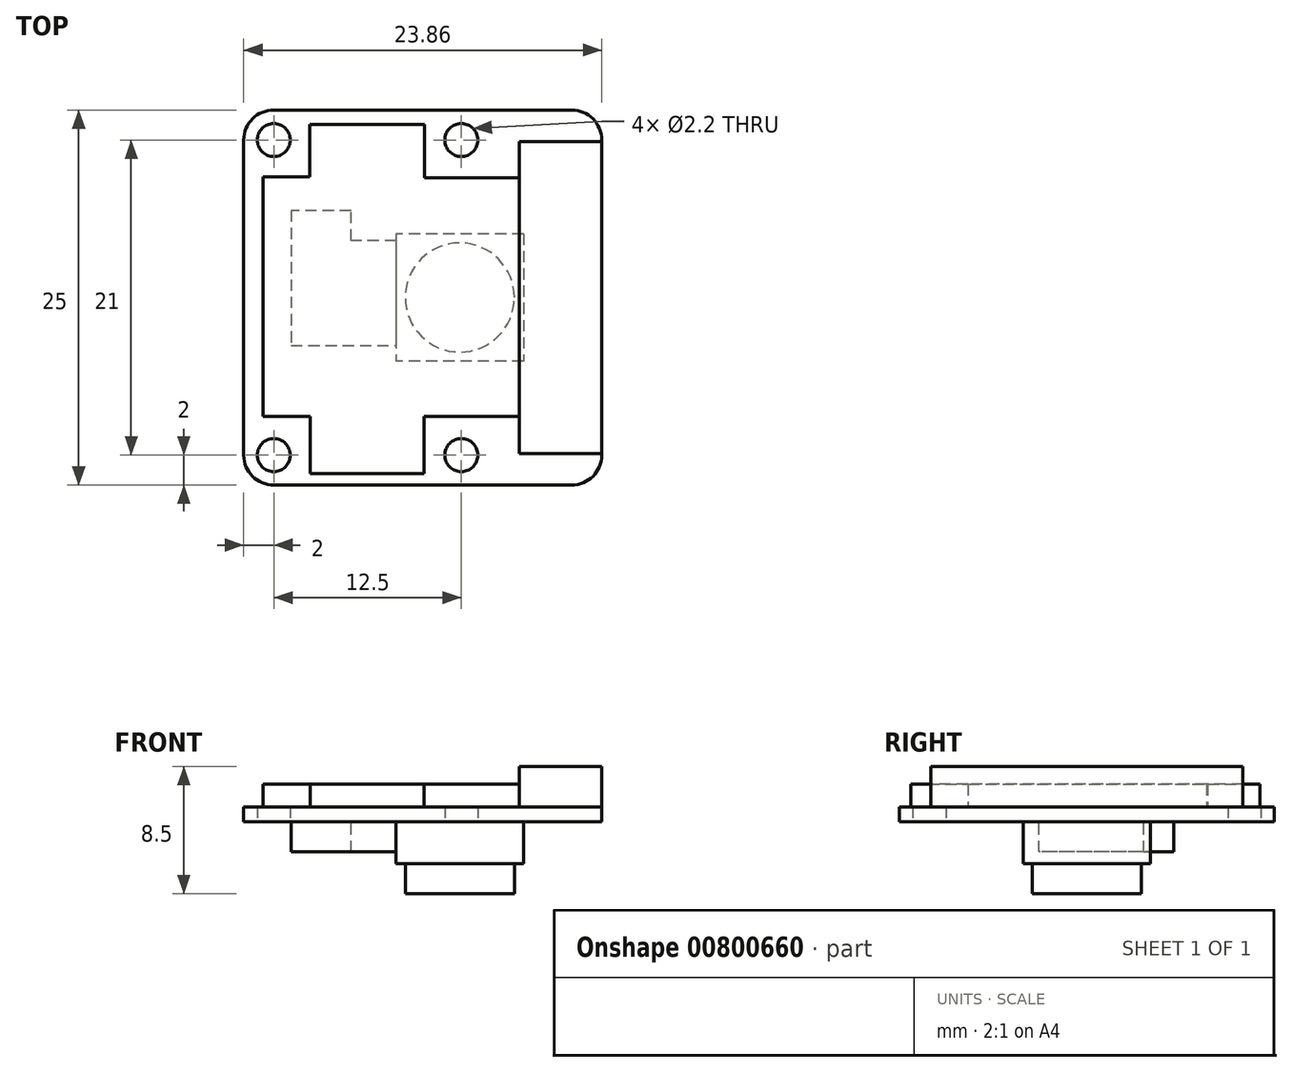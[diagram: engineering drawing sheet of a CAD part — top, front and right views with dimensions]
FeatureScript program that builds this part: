
annotation { "Feature Type Name" : "Feature", "Feature Type Description" : "" }
export const myFeature = defineFeature(function(context is Context, id is Id, definition is map)
    precondition{}
    {
        {
            var Q0;
            Q0=qCreatedBy(makeId("Top.planeOp"),FACE);
            var sketch = newSketch(context, id + "F0", { "sketchPlane" : qUnion([Q0])});
            skLineSegment(sketch, "E0.bottom", {"start": v(2, 25) * mm, "end": v(21.86, 25) * mm});
            skLineSegment(sketch, "E0.top", {"start": v(2, 0) * mm, "end": v(21.86, 0) * mm});
            skLineSegment(sketch, "E0.left", {"start": v(0, 23) * mm, "end": v(0, 2) * mm});
            skLineSegment(sketch, "E0.right", {"start": v(23.86, 23) * mm, "end": v(23.86, 2) * mm});
            skCircle(sketch, "E1", {"center": v(2, 2) * mm, "radius": 1.1 * mm});
            skCircle(sketch, "E2", {"center": v(2, 23) * mm, "radius": 1.1 * mm});
            skCircle(sketch, "E3", {"center": v(14.5, 23) * mm, "radius": 1.1 * mm});
            skCircle(sketch, "E4", {"center": v(14.5, 2) * mm, "radius": 1.1 * mm});
            skPoint(sketch, "E5.visualSharp", {"position": v(0, 0) * mm});
            skArc(sketch, "E5.filletArc", {"start": v(0, 2) * mm, "mid": v(0.59, 0.59) * mm, "end": v(2, 0) * mm});
            skPoint(sketch, "E6.visualSharp", {"position": v(0, 25) * mm});
            skArc(sketch, "E6.filletArc", {"start": v(2, 25) * mm, "mid": v(0.59, 24.41) * mm, "end": v(0, 23) * mm});
            skPoint(sketch, "E7.visualSharp", {"position": v(23.86, 25) * mm});
            skArc(sketch, "E7.filletArc", {"start": v(23.86, 23) * mm, "mid": v(23.28, 24.41) * mm, "end": v(21.86, 25) * mm});
            skPoint(sketch, "E8.visualSharp", {"position": v(23.86, 0) * mm});
            skArc(sketch, "E8.filletArc", {"start": v(21.86, 0) * mm, "mid": v(23.28, 0.59) * mm, "end": v(23.86, 2) * mm});
            skSolve(sketch);
        }
        {
            var Q0;
            Q0=makeQuery(id+"F0.imprint","IMPRINT",FACE,{"disambiguationData":[TD([[makeQuery(id+"F0.imprint","IMPRINT",EDGE,{"derivedFrom":sQuery(id+"F0.wireOp",EDGE,"E0.bottom")}),-1.0]])]});
            extrude(context, id + "F1", {"entities" : qUnion([Q0]), "depth" : 1 * mm, "offsetDistance" : 25 * mm});
        }
        {
            var Q0;
            Q0=makeQuery(id+"F1.opExtrude","CAP_FACE",FACE,{"disambiguationData":[OSD([sQuery(id+"F0.wireOp",EDGE,"E0.bottom"),sQuery(id+"F0.wireOp",EDGE,"E0.top"),sQuery(id+"F0.wireOp",EDGE,"E0.left"),sQuery(id+"F0.wireOp",EDGE,"E0.right"),sQuery(id+"F0.wireOp",EDGE,"E1"),sQuery(id+"F0.wireOp",EDGE,"E2"),sQuery(id+"F0.wireOp",EDGE,"E3"),sQuery(id+"F0.wireOp",EDGE,"E4"),sQuery(id+"F0.wireOp",EDGE,"E5.filletArc"),sQuery(id+"F0.wireOp",EDGE,"E6.filletArc"),sQuery(id+"F0.wireOp",EDGE,"E7.filletArc"),sQuery(id+"F0.wireOp",EDGE,"E8.filletArc")])],"isStart":false});
            var sketch = newSketch(context, id + "F2", { "sketchPlane" : qUnion([Q0])});
            skLineSegment(sketch, "E9.0", {"start": v(23.86, 23) * mm, "end": v(23.86, 2) * mm});
            skLineSegment(sketch, "E10.0", {"start": v(2, 0) * mm, "end": v(21.86, 0) * mm});
            skLineSegment(sketch, "E11.0", {"start": v(0, 23) * mm, "end": v(0, 2) * mm});
            skLineSegment(sketch, "E12.bottom", {"start": v(23.86, 22.9) * mm, "end": v(18.36, 22.9) * mm});
            skLineSegment(sketch, "E12.top", {"start": v(23.86, 2.1) * mm, "end": v(18.36, 2.1) * mm});
            skLineSegment(sketch, "E12.left", {"start": v(23.86, 22.9) * mm, "end": v(23.86, 2.1) * mm});
            skLineSegment(sketch, "E12.right", {"start": v(18.36, 22.9) * mm, "end": v(18.36, 2.1) * mm});
            skPoint(sketch, "E13", {"position": v(23.86, 12.5) * mm});
            skLineSegment(sketch, "E14", {"start": v(1.28, 4.59) * mm, "end": v(1.28, 20.55) * mm});
            skLineSegment(sketch, "E15", {"start": v(1.28, 20.55) * mm, "end": v(4.4, 20.55) * mm});
            skLineSegment(sketch, "E16", {"start": v(4.4, 20.55) * mm, "end": v(4.4, 24.04) * mm});
            skLineSegment(sketch, "E17", {"start": v(4.4, 24.04) * mm, "end": v(12.06, 24.04) * mm});
            skLineSegment(sketch, "E18", {"start": v(12.06, 24.04) * mm, "end": v(12.06, 20.48) * mm});
            skLineSegment(sketch, "E19", {"start": v(12.06, 20.48) * mm, "end": v(18.36, 20.48) * mm});
            skLineSegment(sketch, "E20", {"start": v(18.36, 20.48) * mm, "end": v(18.36, 4.57) * mm});
            skLineSegment(sketch, "E21", {"start": v(18.36, 4.57) * mm, "end": v(12.01, 4.57) * mm});
            skLineSegment(sketch, "E22", {"start": v(12.01, 4.57) * mm, "end": v(12.01, 0.76) * mm});
            skLineSegment(sketch, "E23", {"start": v(12.01, 0.76) * mm, "end": v(4.42, 0.76) * mm});
            skLineSegment(sketch, "E24", {"start": v(4.42, 0.76) * mm, "end": v(4.42, 4.59) * mm});
            skLineSegment(sketch, "E25", {"start": v(4.42, 4.59) * mm, "end": v(1.28, 4.59) * mm});
            skCircle(sketch, "E26.0", {"center": v(2, 2) * mm, "radius": 1.1 * mm, "construction": true});
            skCircle(sketch, "E27.0", {"center": v(2, 23) * mm, "radius": 1.1 * mm, "construction": true});
            skCircle(sketch, "E28.0", {"center": v(14.5, 23) * mm, "radius": 1.1 * mm, "construction": true});
            skCircle(sketch, "E29.0", {"center": v(14.5, 2) * mm, "radius": 1.1 * mm, "construction": true});
            skCircle(sketch, "E30", {"center": v(2, 2) * mm, "radius": 2.25 * mm, "construction": true});
            skCircle(sketch, "E31", {"center": v(14.5, 2) * mm, "radius": 2.25 * mm, "construction": true});
            skCircle(sketch, "E32", {"center": v(14.5, 23) * mm, "radius": 2.25 * mm, "construction": true});
            skCircle(sketch, "E33", {"center": v(2, 23) * mm, "radius": 2.25 * mm, "construction": true});
            skSolve(sketch);
        }
        {
            var Q0;
            Q0=makeQuery(id+"F2.imprint","IMPRINT",FACE,{"disambiguationData":[TD([[makeQuery(id+"F2.imprint","IMPRINT",EDGE,{"derivedFrom":sQuery(id+"F2.wireOp",EDGE,"E12.bottom")}),1.0]])]});
            extrude(context, id + "F3", {"entities" : qUnion([Q0]), "depth" : 2.7 * mm, "offsetDistance" : 25 * mm});
        }
        {
            var Q0;
            Q0=makeQuery(id+"F1.opExtrude","CAP_FACE",FACE,{"disambiguationData":[OSD([sQuery(id+"F0.wireOp",EDGE,"E0.bottom"),sQuery(id+"F0.wireOp",EDGE,"E0.top"),sQuery(id+"F0.wireOp",EDGE,"E0.left"),sQuery(id+"F0.wireOp",EDGE,"E0.right"),sQuery(id+"F0.wireOp",EDGE,"E1"),sQuery(id+"F0.wireOp",EDGE,"E2"),sQuery(id+"F0.wireOp",EDGE,"E3"),sQuery(id+"F0.wireOp",EDGE,"E4"),sQuery(id+"F0.wireOp",EDGE,"E5.filletArc"),sQuery(id+"F0.wireOp",EDGE,"E6.filletArc"),sQuery(id+"F0.wireOp",EDGE,"E7.filletArc"),sQuery(id+"F0.wireOp",EDGE,"E8.filletArc")])],"isStart":true});
            var sketch = newSketch(context, id + "F4", { "sketchPlane" : qUnion([Q0])});
            skLineSegment(sketch, "E34.bottom", {"start": v(18.65, -16.75) * mm, "end": v(10.15, -16.75) * mm});
            skLineSegment(sketch, "E34.top", {"start": v(18.65, -8.25) * mm, "end": v(10.15, -8.25) * mm});
            skLineSegment(sketch, "E34.left", {"start": v(18.65, -16.75) * mm, "end": v(18.65, -8.25) * mm});
            skLineSegment(sketch, "E34.right", {"start": v(10.15, -16.75) * mm, "end": v(10.15, -8.25) * mm});
            skPoint(sketch, "E34.middle", {"position": v(14.4, -12.5) * mm});
            skLineSegment(sketch, "E35.0", {"start": v(0, -23) * mm, "end": v(0, -2) * mm});
            skLineSegment(sketch, "E36.0", {"start": v(2, 0) * mm, "end": v(21.86, 0) * mm});
            skLineSegment(sketch, "E37.0", {"start": v(23.86, -23) * mm, "end": v(23.86, -2) * mm});
            skLineSegment(sketch, "E38.bottom", {"start": v(10.15, -9.3) * mm, "end": v(7.15, -9.3) * mm});
            skLineSegment(sketch, "E38.top", {"start": v(10.15, -16.3) * mm, "end": v(7.15, -16.3) * mm});
            skLineSegment(sketch, "E38.left", {"start": v(10.15, -9.3) * mm, "end": v(10.15, -16.3) * mm});
            skLineSegment(sketch, "E38.right", {"start": v(7.15, -9.3) * mm, "end": v(7.15, -16.3) * mm});
            skLineSegment(sketch, "E39", {"start": v(7.15, -16.3) * mm, "end": v(7.15, -18.3) * mm});
            skLineSegment(sketch, "E40", {"start": v(7.15, -18.3) * mm, "end": v(3.15, -18.3) * mm});
            skLineSegment(sketch, "E41", {"start": v(3.15, -18.3) * mm, "end": v(3.15, -9.3) * mm});
            skLineSegment(sketch, "E42", {"start": v(3.15, -9.3) * mm, "end": v(7.15, -9.3) * mm});
            skLineSegment(sketch, "E43", {"start": v(5.15, -9.3) * mm, "end": v(5.15, -18.3) * mm, "construction": true});
            skPoint(sketch, "E44", {"position": v(5.15, -13.8) * mm});
            skSolve(sketch);
        }
        {
            var Q0;
            Q0=makeQuery(id+"F4.imprint","IMPRINT",FACE,{"disambiguationData":[TD([[makeQuery(id+"F4.imprint","IMPRINT",EDGE,{"derivedFrom":sQuery(id+"F4.wireOp",EDGE,"E34.bottom")}),-1.0]])]});
            extrude(context, id + "F5", {"entities" : qUnion([Q0]), "depth" : 2.8 * mm, "offsetDistance" : 25 * mm});
        }
        {
            var Q0;
            Q0=makeQuery(id+"F5.opExtrude","CAP_FACE",FACE,{"disambiguationData":[OSD([sQuery(id+"F4.wireOp",EDGE,"E34.bottom"),sQuery(id+"F4.wireOp",EDGE,"E34.top"),sQuery(id+"F4.wireOp",EDGE,"E34.left"),sQuery(id+"F4.wireOp",EDGE,"E34.right")])],"isStart":false});
            var sketch = newSketch(context, id + "F6", { "sketchPlane" : qUnion([Q0])});
            skLineSegment(sketch, "E45.0", {"start": v(18.65, -16.75) * mm, "end": v(18.65, -8.25) * mm});
            skLineSegment(sketch, "E46.0", {"start": v(18.65, -8.25) * mm, "end": v(10.15, -8.25) * mm});
            skCircle(sketch, "E47", {"center": v(14.4, -12.5) * mm, "radius": 3.63 * mm});
            skPoint(sketch, "E47.centerSnap0", {"position": v(18.65, -12.5) * mm});
            skPoint(sketch, "E48", {"position": v(14.4, -8.25) * mm});
            skSolve(sketch);
        }
        {
            var Q0;
            Q0=makeQuery(id+"F6.imprint","IMPRINT",FACE,{"disambiguationData":[TD([[makeQuery(id+"F6.imprint","IMPRINT",EDGE,{"derivedFrom":sQuery(id+"F6.wireOp",EDGE,"E47")}),1.0]])]});
            extrude(context, id + "F7", {"entities" : qUnion([Q0]), "operationType" : NewBodyOperationType.ADD, "depth" : 2 * mm, "offsetDistance" : 25 * mm});
        }
        {
            var Q0;
            Q0=makeQuery(id+"F4.imprint","IMPRINT",FACE,{"disambiguationData":[TD([[makeQuery(id+"F4.imprint","IMPRINT",EDGE,{"derivedFrom":sQuery(id+"F4.wireOp",EDGE,"E38.right")}),-1.0]])]});
            var Q1;
            Q1=makeQuery(id+"F4.imprint","IMPRINT",FACE,{"disambiguationData":[TD([[makeQuery(id+"F4.imprint","IMPRINT",EDGE,{"derivedFrom":sQuery(id+"F4.wireOp",EDGE,"E38.bottom")}),1.0]])]});
            extrude(context, id + "F8", {"entities" : qUnion([Q0, Q1]), "depth" : 2 * mm, "offsetDistance" : 25 * mm});
        }
        {
            var Q0;
            Q0=makeQuery(id+"F2.imprint","IMPRINT",FACE,{"disambiguationData":[TD([[makeQuery(id+"F2.imprint","IMPRINT",EDGE,{"derivedFrom":sQuery(id+"F2.wireOp",EDGE,"E14")}),-1.0]])]});
            extrude(context, id + "F9", {"entities" : qUnion([Q0]), "depth" : 1.5 * mm, "offsetDistance" : 25 * mm});
        }
    });
